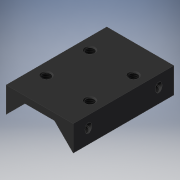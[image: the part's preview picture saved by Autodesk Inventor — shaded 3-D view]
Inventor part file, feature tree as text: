
AUTODESK INVENTOR PART (.ipt)
format: ipt  version: 2019 (Build 230136000, 136)  size: 212,480 bytes
history: native  units: mm
features: other x42, sketch x7, revolve x6, thread x6, pattern_linear x2, extrude x1
ambient origin geometry x8: Origin, YZ Plane, XZ Plane, XY Plane, X Axis, Y Axis, Z Axis, Center Point
bodies: Solid1 (feature_tree)
feature tree (64):
  extrude  "Extrusion1"  TaperAngle=360.0deg  [1 undecoded]
  revolve  "Revolution1"  [1 undecoded]
  thread  "Thread1"  [1 undecoded]
  pattern_linear  "Rectangular Pattern1"  Count1=2 Spacing1=13.0mm
  revolve  "Revolution2"  [1 undecoded]
  thread  "Thread2"  [1 undecoded]
  pattern_linear  "Rectangular Pattern2"  Spacing1=360.0deg  [1 undecoded]
  revolve  "Revolution3"  [1 undecoded]
  thread  "Thread3"  [1 undecoded]
  revolve  "Revolution4"  [1 undecoded]
  thread  "Thread4"  [1 undecoded]
  revolve  "Revolution5"  [1 undecoded]
  thread  "Thread5"  [1 undecoded]
  revolve  "Revolution6"  [1 undecoded]
  thread  "Thread6"  [1 undecoded]
  other  "to_d_XY"
  other  "to_d_YZ"
  other  "to_d_ZX"
  other  "to_d_X"
  other  "to_d_Y"
  other  "to_d_Z"
  other  "to_d_Center"
  other  "to_rail_XY"
  other  "to_rail_YZ"
  other  "to_rail_ZX"
  other  "to_rail_X"
  other  "to_rail_Y"
  other  "to_rail_Z"
  other  "to_rail_Center"
  other  "to_sc1_XY"
  other  "to_sc1_YZ"
  other  "to_sc1_ZX"
  other  "to_sc1_X"
  other  "to_sc1_Y"
  other  "to_sc1_Z"
  other  "to_sc1_Center"
  other  "to_sc12_XY"
  other  "to_sc12_YZ"
  other  "to_sc12_ZX"
  other  "to_sc12_X"
  other  "to_sc12_Y"
  other  "to_sc12_Z"
  other  "to_sc12_Center"
  other  "tosc2_XY"
  other  "tosc2_YZ"
  other  "tosc2_ZX"
  other  "tosc2_X"
  other  "tosc2_Y"
  other  "tosc2_Z"
  other  "tosc2_Center"
  other  "tosc22_XY"
  other  "tosc22_YZ"
  other  "tosc22_ZX"
  other  "tosc22_X"
  other  "tosc22_Y"
  other  "tosc22_Z"
  other  "tosc22_Center"
  sketch  "Sketch_1"  dims[d0=30.0mm d1=0.0mm d2=360.0deg]
  sketch  "Sketch_8"  dims[d26=360.0deg]
  sketch  "Sketch_10"  dims[d27=1.567mm d28=0.0mm d29=360.0deg d30=1.567mm d31=0.0mm d32=0.0mm d33=0.0mm d34=0.0mm d35=0.0mm]
  sketch  "Sketch_2"  dims[d3=5.059mm d4=0.0mm d5=20.0mm d7=13.0mm d8=10.0mm d10=0.0mm d11=360.0deg]
  sketch  "Sketch_4"  dims[d20=360.0deg d21=1.567mm d22=0.0mm d23=360.0deg]
  sketch  "Sketch_3"  dims[d12=5.059mm d13=0.0mm d14=20.0mm d16=13.0mm d17=10.0mm d19=0.0mm]
  sketch  "Sketch_5"  dims[d24=1.567mm d25=0.0mm]
note: 14 required parameter values undecoded (feature->parameter linkage not recoverable at this tier; creation-order binding heuristic only, values carry confidence <= 0.55)